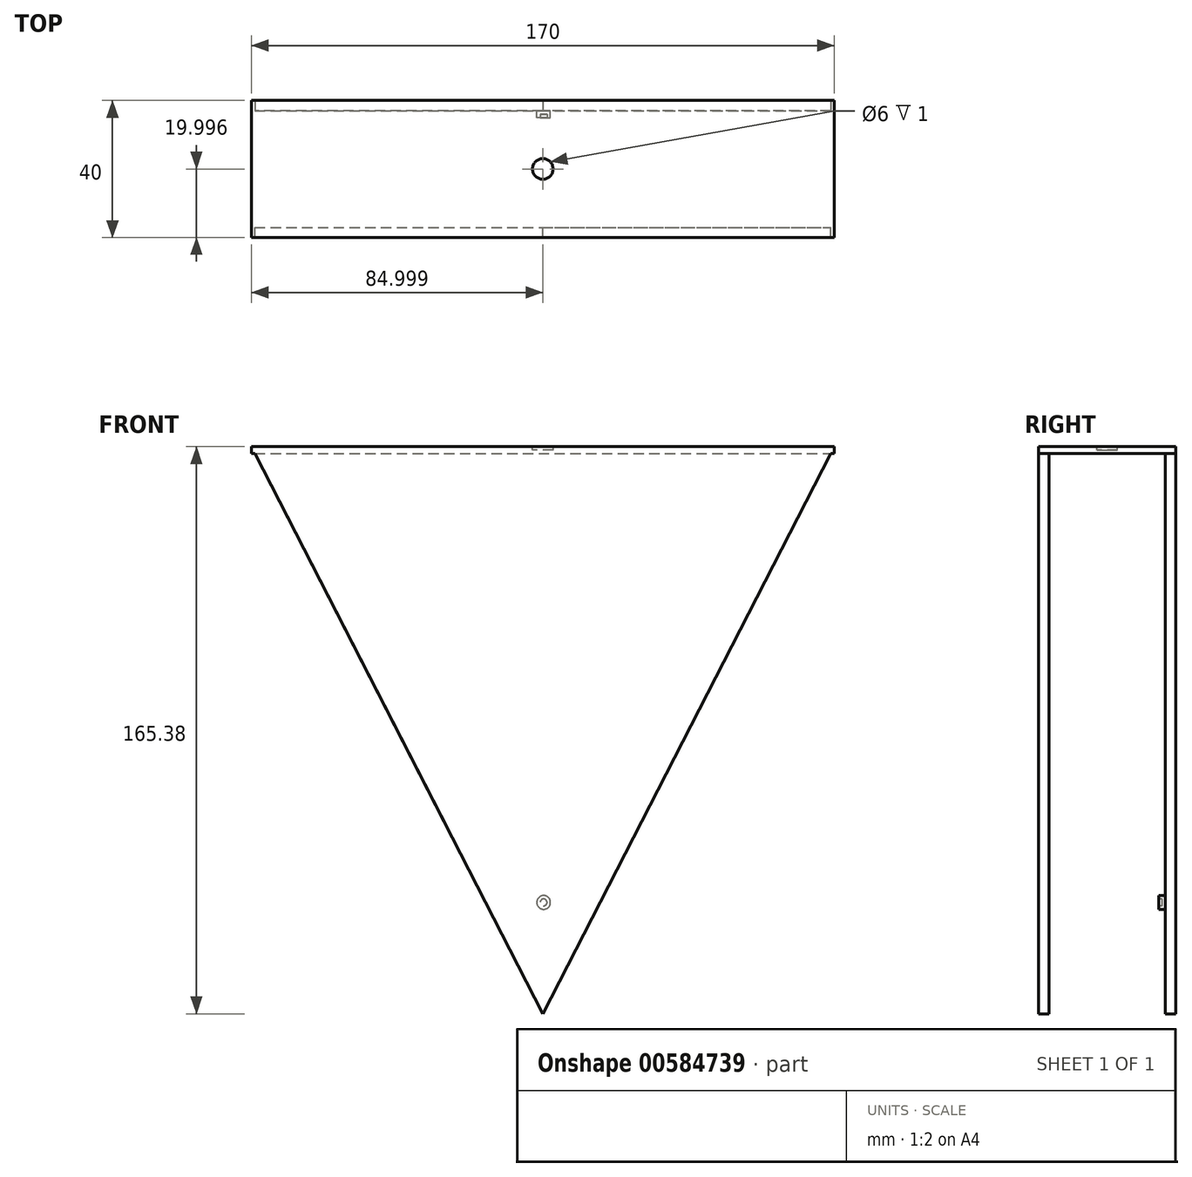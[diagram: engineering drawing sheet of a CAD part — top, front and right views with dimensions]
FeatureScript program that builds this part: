
annotation { "Feature Type Name" : "Feature", "Feature Type Description" : "" }
export const myFeature = defineFeature(function(context is Context, id is Id, definition is map)
    precondition{}
    {
        {
            var Q0;
            Q0=qCreatedBy(makeId("Top.planeOp"),FACE);
            var sketch = newSketch(context, id + "F0", { "sketchPlane" : qUnion([Q0])});
            skLineSegment(sketch, "E0.bottom", {"start": v(-93.24, -13.04) * mm, "end": v(76.76, -13.04) * mm});
            skLineSegment(sketch, "E0.top", {"start": v(-93.24, -47.04) * mm, "end": v(76.76, -47.04) * mm});
            skLineSegment(sketch, "E0.left", {"start": v(-93.24, -13.04) * mm, "end": v(-93.24, -47.04) * mm});
            skLineSegment(sketch, "E0.right", {"start": v(76.76, -13.04) * mm, "end": v(76.76, -47.04) * mm});
            skSolve(sketch);
        }
        {
            var Q0;
            Q0=makeQuery(id+"F0.imprint","IMPRINT",FACE,{"disambiguationData":[TD([[makeQuery(id+"F0.imprint","IMPRINT",EDGE,{"derivedFrom":sQuery(id+"F0.wireOp",EDGE,"E0.bottom")}),-1.0]])]});
            extrude(context, id + "F1", {"entities" : qUnion([Q0]), "depth" : 2 * mm, "offsetDistance" : 25 * mm});
        }
        {
            var Q0;
            Q0=makeQuery(id+"F1.opExtrude","SWEPT_FACE",FACE,{"disambiguationData":[OSD([sQuery(id+"F0.wireOp",EDGE,"E0.top")])]});
            var sketch = newSketch(context, id + "F2", { "sketchPlane" : qUnion([Q0])});
            skLineSegment(sketch, "E1", {"start": v(-8.24, 0) * mm, "end": v(-8.24, -163.38) * mm, "construction": true});
            skSolve(sketch);
        }
        {
            var Q0;
            {var subQ0=sQuery(id+"F0.wireOp",EDGE,"E0.top");Q0=makeQuery(id+"F2.imprint","IMPRINT",FACE,{"disambiguationData":[TD([[makeQuery(id+"F2.imprint","IMPRINT",EDGE,{"derivedFrom":makeQuery(id+"F1.opExtrude","CAP_EDGE",EDGE,{"disambiguationData":[OSD([subQ0])],"isStart":true})}),1.0]])]});}
            var sketch = newSketch(context, id + "F3", { "sketchPlane" : qUnion([Q0])});
            skLineSegment(sketch, "E2", {"start": v(-93.24, 2) * mm, "end": v(-8.24, -163.38) * mm});
            skLineSegment(sketch, "E3", {"start": v(-8.24, -163.38) * mm, "end": v(76.76, 2) * mm});
            skLineSegment(sketch, "E4", {"start": v(76.76, 2) * mm, "end": v(-93.24, 2) * mm});
            skSolve(sketch);
        }
        {
            var Q0;
            {var subQ0=sQuery(id+"F3.wireOp",EDGE,"E3");var subQ1=sQuery(id+"F3.wireOp",EDGE,"E2");var subQ2=makeQuery(id+"F3.imprint","INTERSECT",VERTEX,{"derivedFrom":[subQ1,subQ0]});Q0=makeQuery(id+"F3.imprint","IMPRINT",FACE,{"disambiguationData":[TD([[makeQuery(id+"F3.imprint","IMPRINT",EDGE,{"disambiguationData":[TD([[subQ2,1.0]])],"derivedFrom":subQ1}),1.0]])]});}
            var Q1;
            {var subQ0=sQuery(id+"F0.wireOp",EDGE,"E0.top");Q1=makeQuery(id+"F2.imprint","IMPRINT",FACE,{"disambiguationData":[TD([[makeQuery(id+"F2.imprint","IMPRINT",EDGE,{"derivedFrom":makeQuery(id+"F1.opExtrude","CAP_EDGE",EDGE,{"disambiguationData":[OSD([subQ0])],"isStart":true})}),1.0]])]});}
            extrude(context, id + "F4", {"entities" : qUnion([Q0, Q1]), "operationType" : NewBodyOperationType.ADD, "depth" : 3 * mm, "offsetDistance" : 25 * mm});
        }
        {
            var Q0;
            Q0=makeQuery(id+"F1.opExtrude","SWEPT_FACE",FACE,{"disambiguationData":[OSD([sQuery(id+"F0.wireOp",EDGE,"E0.bottom")])]});
            var sketch = newSketch(context, id + "F5", { "sketchPlane" : qUnion([Q0])});
            skLineSegment(sketch, "E5", {"start": v(8.24, 0) * mm, "end": v(8.24, -163.1) * mm, "construction": true});
            skSolve(sketch);
        }
        {
            var Q0;
            {var subQ0=sQuery(id+"F0.wireOp",EDGE,"E0.bottom");Q0=makeQuery(id+"F5.imprint","IMPRINT",FACE,{"disambiguationData":[TD([[makeQuery(id+"F5.imprint","IMPRINT",EDGE,{"derivedFrom":makeQuery(id+"F1.opExtrude","CAP_EDGE",EDGE,{"disambiguationData":[OSD([subQ0])],"isStart":true})}),-1.0]])]});}
            var sketch = newSketch(context, id + "F6", { "sketchPlane" : qUnion([Q0])});
            skLineSegment(sketch, "E6", {"start": v(-76.76, 2) * mm, "end": v(8.24, -163.38) * mm});
            skLineSegment(sketch, "E7", {"start": v(8.24, -163.38) * mm, "end": v(93.24, 2) * mm});
            skLineSegment(sketch, "E8", {"start": v(93.24, 2) * mm, "end": v(-76.76, 2) * mm});
            skSolve(sketch);
        }
        {
            var Q0;
            {var subQ0=sQuery(id+"F6.wireOp",EDGE,"E7");var subQ1=sQuery(id+"F6.wireOp",EDGE,"E6");var subQ2=makeQuery(id+"F6.imprint","INTERSECT",VERTEX,{"derivedFrom":[subQ1,subQ0]});Q0=makeQuery(id+"F6.imprint","IMPRINT",FACE,{"disambiguationData":[TD([[makeQuery(id+"F6.imprint","IMPRINT",EDGE,{"disambiguationData":[TD([[subQ2,1.0]])],"derivedFrom":subQ1}),1.0]])]});}
            var Q1;
            {var subQ0=sQuery(id+"F0.wireOp",EDGE,"E0.bottom");Q1=makeQuery(id+"F5.imprint","IMPRINT",FACE,{"disambiguationData":[TD([[makeQuery(id+"F5.imprint","IMPRINT",EDGE,{"derivedFrom":makeQuery(id+"F1.opExtrude","CAP_EDGE",EDGE,{"disambiguationData":[OSD([subQ0])],"isStart":true})}),-1.0]])]});}
            extrude(context, id + "F7", {"entities" : qUnion([Q0, Q1]), "operationType" : NewBodyOperationType.ADD, "depth" : 3 * mm, "offsetDistance" : 25 * mm});
        }
        {
            var Q0;
            {var subQ0=sQuery(id+"F0.wireOp",EDGE,"E0.bottom");Q0=makeQuery(id+"F7.boolean.opBoolean","MERGE",FACE,{"derivedFrom":[makeQuery(id+"F7.opExtrude","CAP_FACE",FACE,{"disambiguationData":[OSD([subQ0,sQuery(id+"F0.wireOp",EDGE,"E0.left"),sQuery(id+"F0.wireOp",EDGE,"E0.right")])],"isStart":true}),makeQuery(id+"F7.opExtrude","CAP_FACE",FACE,{"disambiguationData":[OSD([subQ0,sQuery(id+"F6.wireOp",EDGE,"E6"),sQuery(id+"F6.wireOp",EDGE,"E7")])],"isStart":true})]});}
            var sketch = newSketch(context, id + "F8", { "sketchPlane" : qUnion([Q0])});
            skCircle(sketch, "E9", {"center": v(-8, -130.91) * mm, "radius": 2 * mm});
            skSolve(sketch);
        }
        {
            var Q0;
            Q0=qSketchRegion(id+"F8",true);
            extrude(context, id + "F9", {"entities" : qUnion([Q0]), "operationType" : NewBodyOperationType.ADD, "depth" : 2 * mm, "offsetDistance" : 25 * mm});
        }
        {
            var Q0;
            Q0=makeQuery(id+"F9.opExtrude","CAP_FACE",FACE,{"disambiguationData":[OSD([sQuery(id+"F8.wireOp",EDGE,"E9")])],"isStart":false});
            var sketch = newSketch(context, id + "F10", { "sketchPlane" : qUnion([Q0])});
            skCircle(sketch, "E10", {"center": v(-8, -130.91) * mm, "radius": 1 * mm});
            skSolve(sketch);
        }
        {
            var Q0;
            Q0=makeQuery(id+"F10.imprint","IMPRINT",FACE,{"disambiguationData":[TD([[makeQuery(id+"F10.imprint","IMPRINT",EDGE,{"derivedFrom":sQuery(id+"F10.wireOp",EDGE,"E10")}),1.0]])]});
            extrude(context, id + "F11", {"entities" : qUnion([Q0]), "operationType" : NewBodyOperationType.REMOVE, "oppositeDirection" : true, "depth" : 1 * mm, "offsetDistance" : 25 * mm});
        }
        {
            var Q0;
            {var subQ0=sQuery(id+"F0.wireOp",EDGE,"E0.bottom");var subQ1=sQuery(id+"F0.wireOp",EDGE,"E0.top");Q0=makeQuery(id+"F7.boolean.opBoolean","MERGE",FACE,{"derivedFrom":[makeQuery(id+"F4.boolean.opBoolean","MERGE",FACE,{"derivedFrom":[makeQuery(id+"F1.opExtrude","CAP_FACE",FACE,{"disambiguationData":[OSD([subQ0,subQ1,sQuery(id+"F0.wireOp",EDGE,"E0.left"),sQuery(id+"F0.wireOp",EDGE,"E0.right")])],"isStart":false}),makeQuery(id+"F4.opExtrude","SWEPT_FACE",FACE,{"disambiguationData":[OSD([subQ1]),TDD([makeQuery(id+"F2.imprint","IMPRINT",EDGE,{"derivedFrom":makeQuery(id+"F1.opExtrude","CAP_EDGE",EDGE,{"disambiguationData":[OSD([subQ1])],"isStart":false})})])]})]}),makeQuery(id+"F7.opExtrude","SWEPT_FACE",FACE,{"disambiguationData":[OSD([subQ0]),TDD([makeQuery(id+"F5.imprint","IMPRINT",EDGE,{"derivedFrom":makeQuery(id+"F1.opExtrude","CAP_EDGE",EDGE,{"disambiguationData":[OSD([subQ0])],"isStart":false})})])]})]});}
            var sketch = newSketch(context, id + "F12", { "sketchPlane" : qUnion([Q0])});
            skCircle(sketch, "E11", {"center": v(-8.24, -30.04) * mm, "radius": 3 * mm});
            skSolve(sketch);
        }
        {
            var Q0;
            Q0=makeQuery(id+"F12.imprint","IMPRINT",FACE,{"disambiguationData":[TD([[makeQuery(id+"F12.imprint","IMPRINT",EDGE,{"derivedFrom":sQuery(id+"F12.wireOp",EDGE,"E11")}),1.0]])]});
            extrude(context, id + "F13", {"entities" : qUnion([Q0]), "operationType" : NewBodyOperationType.REMOVE, "oppositeDirection" : true, "depth" : 1 * mm, "offsetDistance" : 25 * mm});
        }
    });
